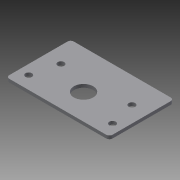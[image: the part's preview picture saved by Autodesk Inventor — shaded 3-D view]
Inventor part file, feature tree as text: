
AUTODESK INVENTOR PART (.ipt)
format: ipt  version: 2013 (Build 170138000, 138)  size: 111,616 bytes
history: native  units: in
note: dims shown in document units (in); Inventor stores cm internally (conversion verified against a paired STEP export)
features: sketch x3, hole x2, extrude x1
ambient origin geometry x8: Origin, YZ Plane, XZ Plane, XY Plane, X Axis, Y Axis, Z Axis, Center Point
bodies: Solid1 (feature_tree)
feature tree (6):
  extrude  "Extrusion1"  Depth=2.5in
  hole  "Hole1"  [1 undecoded]
  hole  "Hole2"  [1 undecoded]
  sketch  "Sketch1"  dims[d0=4.0in d1=2.5in]
  sketch  "Sketch2"  dims[d2=0.125in d3=0.0in d4=2.0in]
  sketch  "Sketch3"  dims[d5=1.5in d6=0.75in d7=0.75in d8=0.375in d9=0.25in d10=0.5635in d11=1.0in d12=0.8108in d13=0.125in d22=0.25in d23=0.75in d24=0.375in d25=0.25in d26=0.5635in d27=1.0in d28=0.8108in d29=2.0in d30=0.25in d33=1.0in d36=0.375in d37=0.375in d38=0.25in d39=0.5in d40=3.25in]
note: 2 required parameter values undecoded (feature->parameter linkage not recoverable at this tier; creation-order binding heuristic only, values carry confidence <= 0.55)
